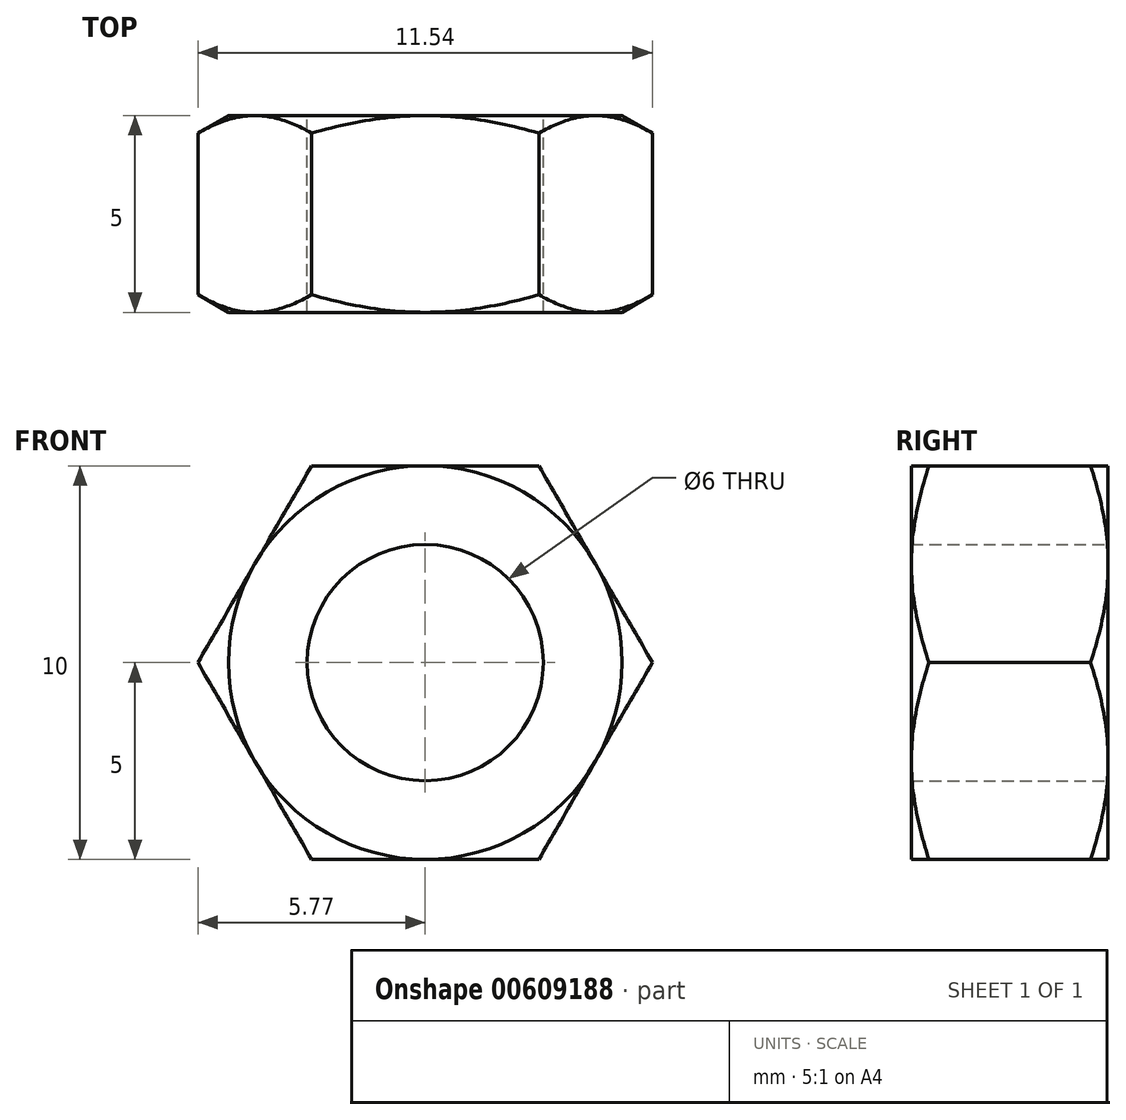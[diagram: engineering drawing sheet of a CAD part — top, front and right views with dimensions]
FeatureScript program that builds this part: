
annotation { "Feature Type Name" : "Feature", "Feature Type Description" : "" }
export const myFeature = defineFeature(function(context is Context, id is Id, definition is map)
    precondition{}
    {
        {
            var Q0;
            Q0=qCreatedBy(makeId("Front.planeOp"),FACE);
            var sketch = newSketch(context, id + "F0", { "sketchPlane" : qUnion([Q0])});
            skCircle(sketch, "E0", {"center": v(0, 0) * mm, "radius": 3 * mm});
            skCircle(sketch, "E1.cCircle", {"center": v(0, 0) * mm, "radius": 5 * mm, "construction": true});
            skLineSegment(sketch, "E1.0", {"start": v(-2.89, 5) * mm, "end": v(2.89, 5) * mm});
            skLineSegment(sketch, "E1.1", {"start": v(2.89, 5) * mm, "end": v(5.77, 0) * mm});
            skLineSegment(sketch, "E1.2", {"start": v(5.77, 0) * mm, "end": v(2.89, -5) * mm});
            skLineSegment(sketch, "E1.3", {"start": v(2.89, -5) * mm, "end": v(-2.89, -5) * mm});
            skLineSegment(sketch, "E1.4", {"start": v(-2.89, -5) * mm, "end": v(-5.77, 0) * mm});
            skLineSegment(sketch, "E1.5", {"start": v(-5.77, 0) * mm, "end": v(-2.89, 5) * mm});
            skPoint(sketch, "E1.0.midPoint", {"position": v(0, 5) * mm});
            skCircle(sketch, "E2", {"center": v(0, 0) * mm, "radius": 5.77 * mm, "construction": true});
            skSolve(sketch);
        }
        {
            var Q0;
            Q0 = qSketchRegion(id + "F0", true);
            extrude(context, id + "F1", {"entities" : qUnion([Q0]), "depth" : 5 * mm, "offsetDistance" : 25 * mm});
        }
        {
            var Q0;
            Q0=qCreatedBy(makeId("Right.planeOp"),FACE);
            var sketch = newSketch(context, id + "F2", { "sketchPlane" : qUnion([Q0])});
            skLineSegment(sketch, "E3", {"start": v(-0.46, 5.8) * mm, "end": v(0, 5) * mm});
            skLineSegment(sketch, "E4", {"start": v(-5, 5.8) * mm, "end": v(-5, 5) * mm});
            skLineSegment(sketch, "E5", {"start": v(-5, 5) * mm, "end": v(-4.54, 5.8) * mm});
            skLineSegment(sketch, "E6", {"start": v(-4.54, 5.8) * mm, "end": v(-5, 5.8) * mm});
            skLineSegment(sketch, "E7", {"start": v(0, 0) * mm, "end": v(-5.03, 0) * mm, "construction": true});
            skLineSegment(sketch, "E8", {"start": v(-0.46, 5.8) * mm, "end": v(0, 5.8) * mm});
            skLineSegment(sketch, "E9", {"start": v(0, 5.8) * mm, "end": v(0, 5) * mm});
            skSolve(sketch);
        }
        {
            var Q0;
            Q0 = qSketchRegion(id + "F2", true);
            var Q1;
            Q1=sQuery(id+"F2.wireOp",EDGE,"E7");
            revolve(context, id + "F3", {"operationType" : NewBodyOperationType.REMOVE, "entities" : qUnion([Q0]), "axis" : qUnion([Q1]), "revolveType" : RevolveType.FULL, "oppositeDirection" : true});
        }
    });
